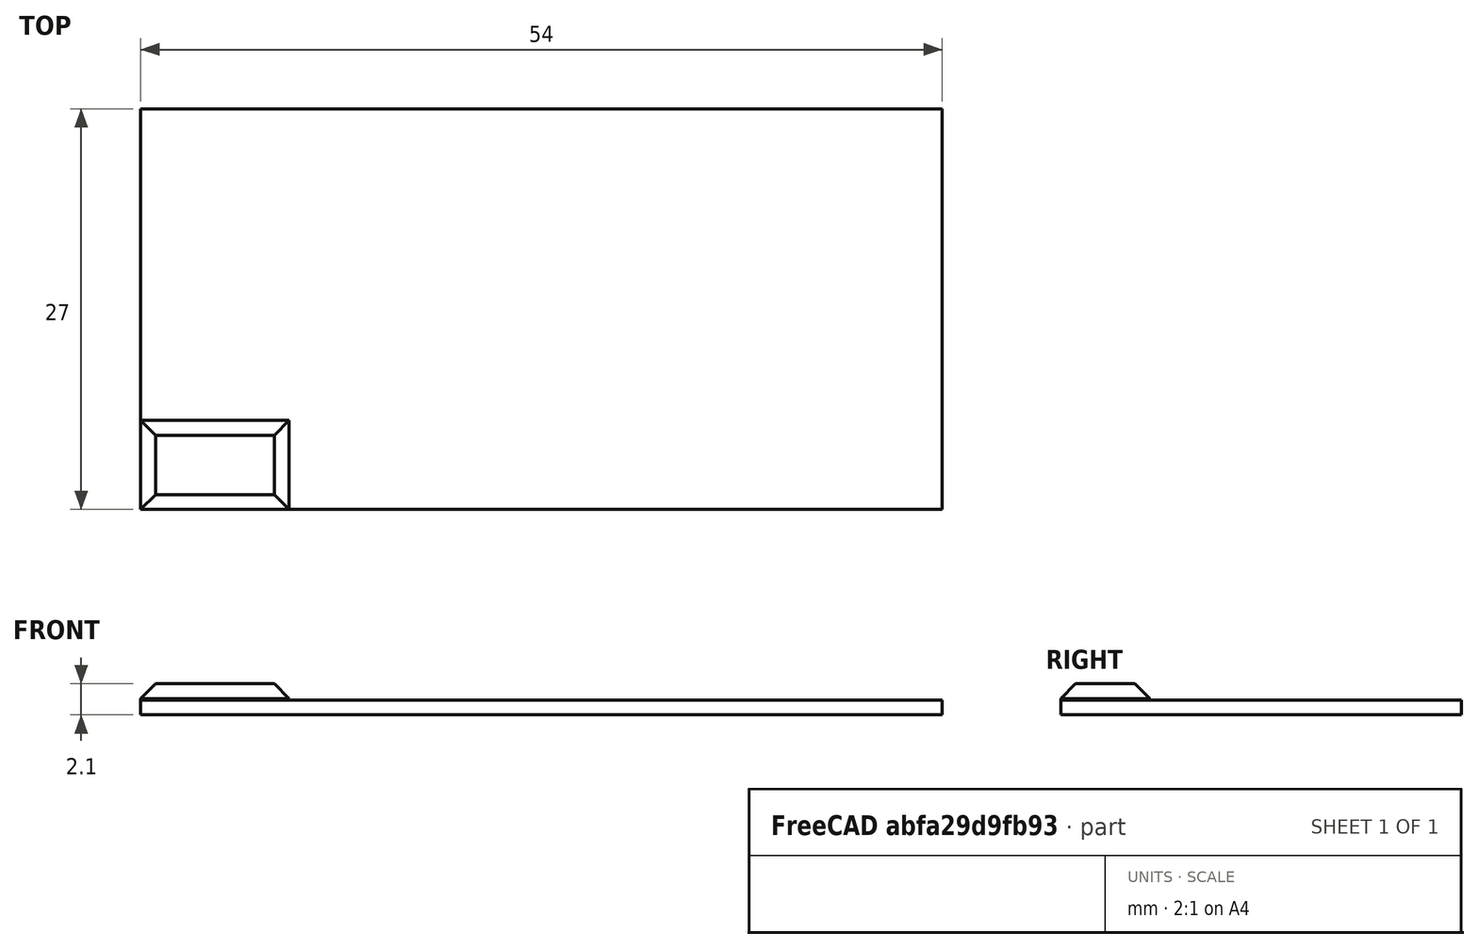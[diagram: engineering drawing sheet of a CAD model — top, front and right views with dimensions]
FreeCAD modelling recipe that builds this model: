
FCSTD DOCUMENT  (FreeCAD 0.21R33694 (Git))
Label: OJT1_T12R02_xocolata
License: All rights reserved
LicenseURL: https://en.wikipedia.org/wiki/All_rights_reserved
objects: Part::Box×2, Part::Chamfer×1, Part::FeaturePython×1
note: 3 computed .brp shape members not serialized (recipe doc carries the construction recipe); baked Part::Feature solids carry a one-line shape summary decoded from their .brp

FEATURE [Part::Box] Box  label="base"
  AttacherType = Attacher::AttachEngine3D
  Height = 1
  Length = 54
  Width = 27
FEATURE [Part::Box] Box001  label="quadrat_petit"
  AttacherType = Attacher::AttachEngine3D
  Height = 1.1
  Length = 10
  Placement = pos=(0,0,1) rot=(0,0,1;0rad)
  Width = 6
FEATURE [Part::Chamfer] Chamfer  label="porció petita"
  Base = -> Box001
  Edges = 4 edges r=1: [Edge2,Edge6,Edge10,Edge12]
FEATURE [Part::FeaturePython] Array  # Draft array (typed FeaturePython)
  AlwaysSyncPlacement = false
  Angle = 360
  ArrayType = 0
  Axis = (0,0,1)
  Base = -> Chamfer
  Center = (0,0,0)
  Count = 20
  ExpandArray = false
  Fuse = false
  IntervalAxis = (0,0,0)
  IntervalX = (11,0,0)
  IntervalY = (0,7,0)
  IntervalZ = (0,0,100)
  NumberCircles = 3
  NumberPolar = 5
  NumberX = 5
  NumberY = 4
  NumberZ = 1
  PlacementList = 20 placements: [(0,0,0),(0,7,0),(0,14,0),(0,21,0),(11,0,0),(11,7,0),(11,14,0),(11,21,0),(22,0,0),(22,7,0),(22,14,0),(22,21,0),(33,0,0),(33,7,0),(33,14,0),(33,21,0),(44,0,0),(44,7,0),(44,14,0),(44,21,0)]
  RadialDistance = 50
  ScaleList = (20) [(1,1,1),(1,1,1),(1,1,1),(1,1,1),(1,1,1),(1,1,1),(1,1,1),(1,1,1),(1,1,1),(1,1,1),(1,1,1),(1,1,1),(1,1,1),(1,1,1),(1,1,1),(1,1,1),(1,1,1),(1,1,1),(1,1,1),(1,1,1)]
  Symmetry = 1
  TangentialDistance = 25
